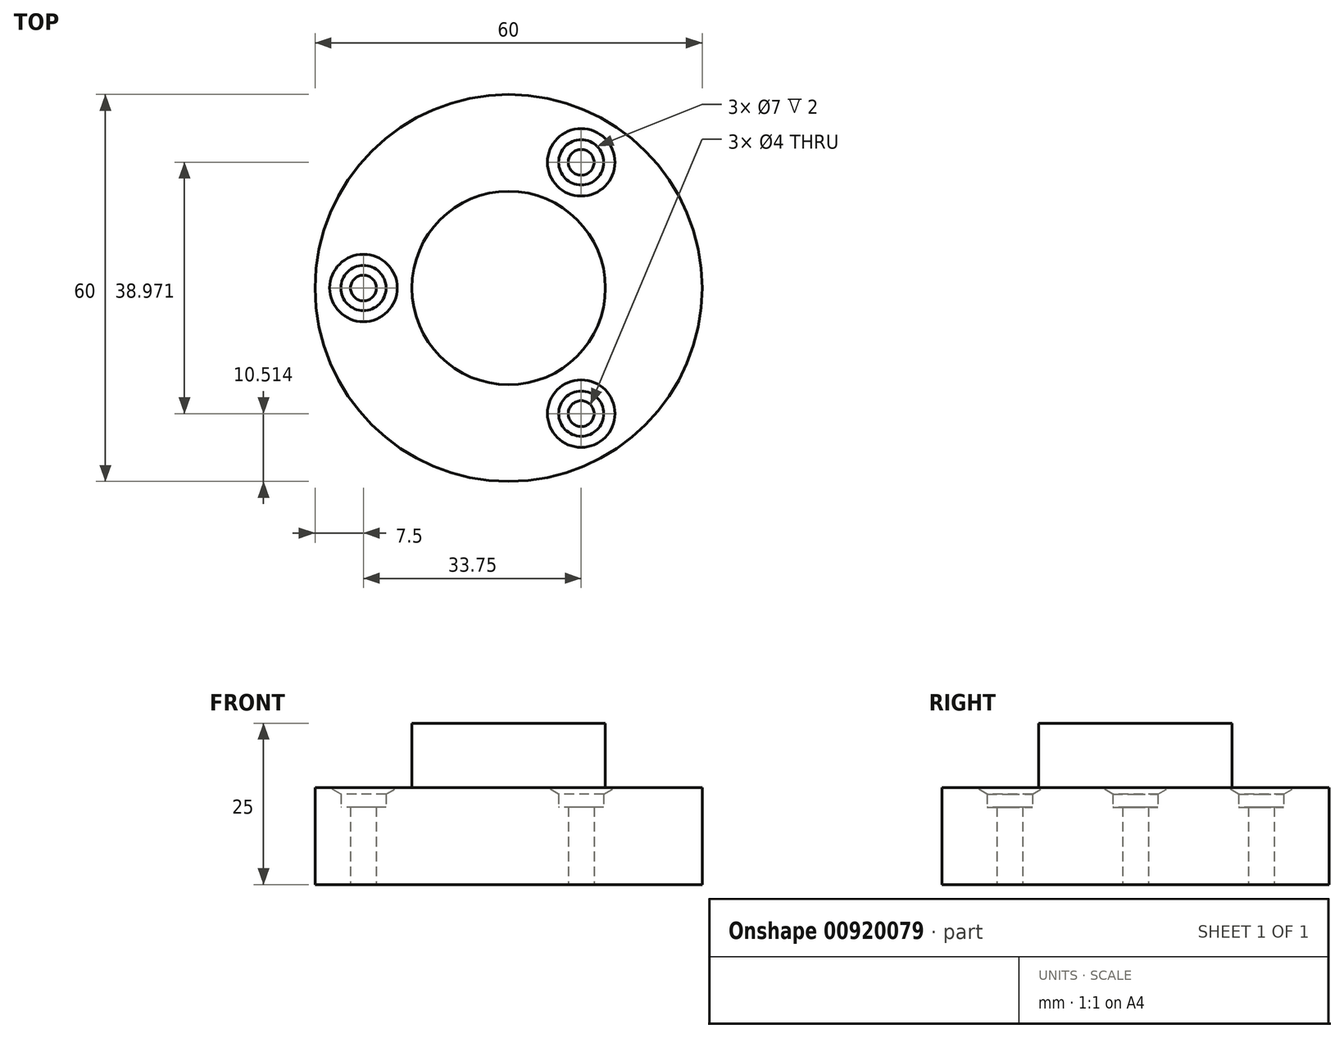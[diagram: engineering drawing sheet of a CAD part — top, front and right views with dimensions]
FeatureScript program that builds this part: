
annotation { "Feature Type Name" : "Feature", "Feature Type Description" : "" }
export const myFeature = defineFeature(function(context is Context, id is Id, definition is map)
    precondition{}
    {
        {
            var Q0;
            Q0=qCreatedBy(makeId("Top.planeOp"),FACE);
            var sketch = newSketch(context, id + "F0", { "sketchPlane" : qUnion([Q0])});
            skCircle(sketch, "E0", {"center": v(0, 0) * mm, "radius": 30 * mm});
            skCircle(sketch, "E1", {"center": v(0, 0) * mm, "radius": 15 * mm});
            skCircle(sketch, "E2", {"center": v(-22.5, 0) * mm, "radius": 2 * mm});
            skLineSegment(sketch, "E3", {"start": v(0, 0) * mm, "end": v(19.36, 33.53) * mm, "construction": true});
            skCircle(sketch, "E4", {"center": v(11.25, 19.49) * mm, "radius": 2 * mm});
            skLineSegment(sketch, "E5", {"start": v(0, 0) * mm, "end": v(22.5, -38.97) * mm, "construction": true});
            skCircle(sketch, "E6", {"center": v(11.25, -19.49) * mm, "radius": 2 * mm});
            skCircle(sketch, "E7", {"center": v(0, 0) * mm, "radius": 22.5 * mm, "construction": true});
            skCircle(sketch, "E8", {"center": v(11.25, -19.49) * mm, "radius": 3.5 * mm});
            skCircle(sketch, "E9.1.0", {"center": v(-22.5, 0) * mm, "radius": 3.5 * mm});
            skCircle(sketch, "E9.2.0", {"center": v(11.25, 19.49) * mm, "radius": 3.5 * mm});
            skLineSegment(sketch, "E9.anchor1", {"start": v(0, 0) * mm, "end": v(11.25, -19.49) * mm, "construction": true});
            skLineSegment(sketch, "E9.anchor2", {"start": v(0, 0) * mm, "end": v(11.25, 19.49) * mm, "construction": true});
            skSolve(sketch);
        }
        {
            var Q0;
            Q0=makeQuery(id+"F0.imprint","IMPRINT",FACE,{"disambiguationData":[TD([[makeQuery(id+"F0.imprint","IMPRINT",EDGE,{"derivedFrom":sQuery(id+"F0.wireOp",EDGE,"E0")}),1.0]])]});
            extrude(context, id + "F1", {"entities" : qUnion([Q0]), "depth" : 15 * mm, "offsetDistance" : 25 * mm});
        }
        {
            var Q0;
            Q0=makeQuery(id+"F0.imprint","IMPRINT",FACE,{"disambiguationData":[TD([[makeQuery(id+"F0.imprint","IMPRINT",EDGE,{"derivedFrom":sQuery(id+"F0.wireOp",EDGE,"E1")}),1.0]])]});
            extrude(context, id + "F2", {"entities" : qUnion([Q0]), "operationType" : NewBodyOperationType.ADD, "depth" : 25 * mm, "offsetDistance" : 25 * mm});
        }
        {
            var Q0;
            Q0=makeQuery(id+"F0.imprint","IMPRINT",FACE,{"disambiguationData":[TD([[makeQuery(id+"F0.imprint","IMPRINT",EDGE,{"derivedFrom":sQuery(id+"F0.wireOp",EDGE,"E4")}),-1.0]])]});
            var Q1;
            Q1=makeQuery(id+"F0.imprint","IMPRINT",FACE,{"disambiguationData":[TD([[makeQuery(id+"F0.imprint","IMPRINT",EDGE,{"derivedFrom":sQuery(id+"F0.wireOp",EDGE,"E6")}),-1.0]])]});
            var Q2;
            Q2=makeQuery(id+"F0.imprint","IMPRINT",FACE,{"disambiguationData":[TD([[makeQuery(id+"F0.imprint","IMPRINT",EDGE,{"derivedFrom":sQuery(id+"F0.wireOp",EDGE,"E2")}),-1.0]])]});
            extrude(context, id + "F3", {"entities" : qUnion([Q0, Q1, Q2]), "operationType" : NewBodyOperationType.ADD, "depth" : 12 * mm, "offsetDistance" : 25 * mm});
        }
        {
            var Q0;
            Q0=makeQuery(id+"F1.opExtrude","CAP_EDGE",EDGE,{"disambiguationData":[OSD([sQuery(id+"F0.wireOp",EDGE,"E9.1.0")])],"isStart":false});
            var Q1;
            Q1=makeQuery(id+"F1.opExtrude","CAP_EDGE",EDGE,{"disambiguationData":[OSD([sQuery(id+"F0.wireOp",EDGE,"E8")])],"isStart":false});
            var Q2;
            Q2=makeQuery(id+"F1.opExtrude","CAP_EDGE",EDGE,{"disambiguationData":[OSD([sQuery(id+"F0.wireOp",EDGE,"E9.2.0")])],"isStart":false});
            chamfer(context, id + "F4", {"entities" : qUnion([Q0, Q1, Q2]), "chamferType" : ChamferType.OFFSET_ANGLE, "width" : 1 * mm, "oppositeDirection" : false, "angle" : 60 * degree});
        }
    });
